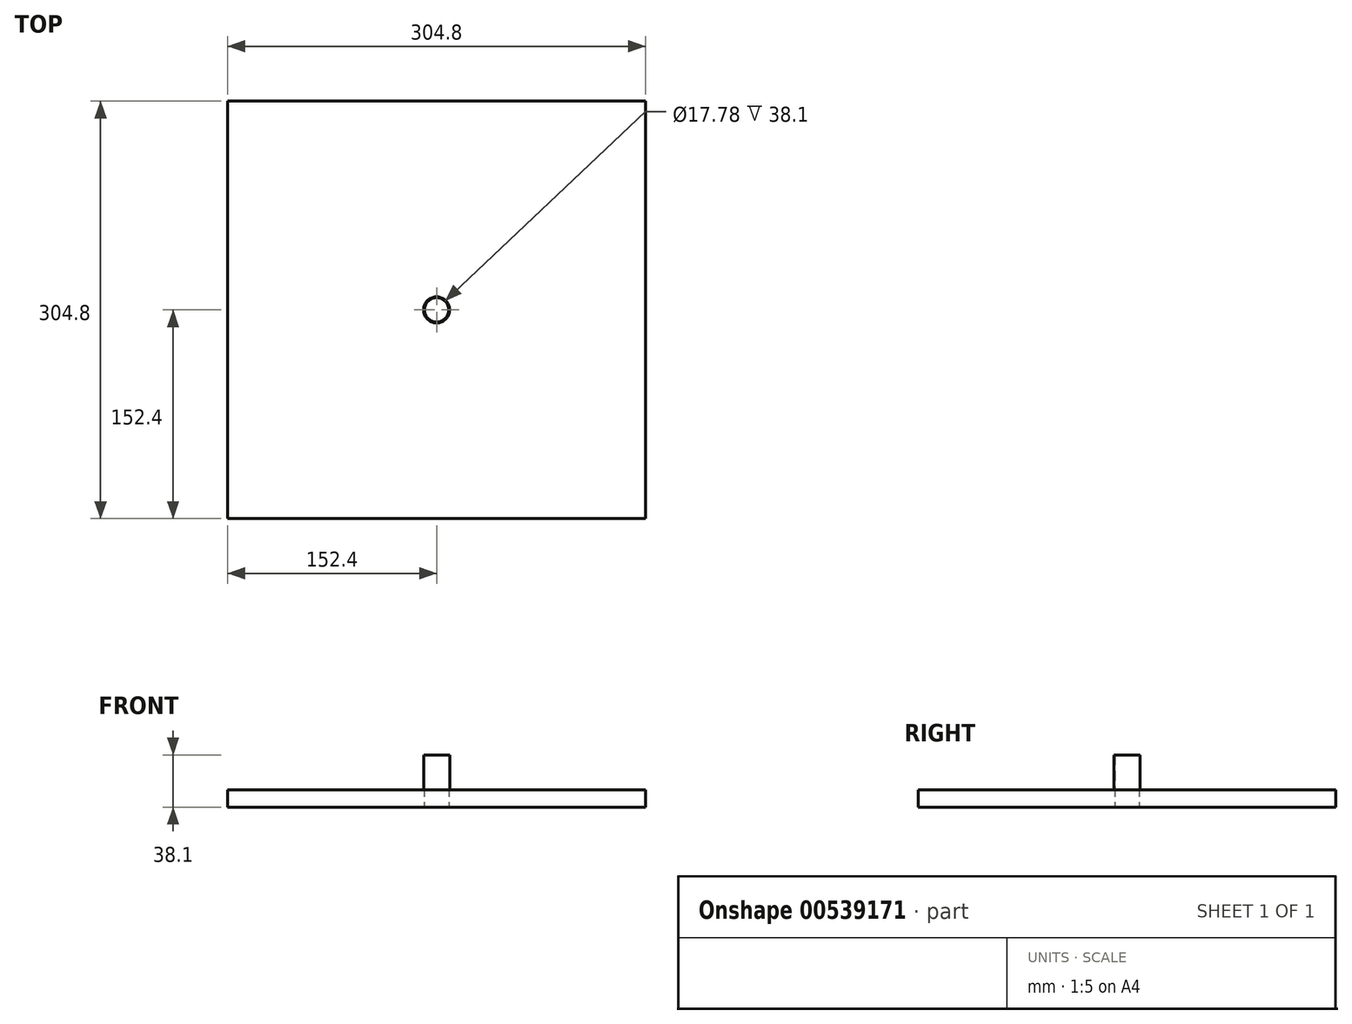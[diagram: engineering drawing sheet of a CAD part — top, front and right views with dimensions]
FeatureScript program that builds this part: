
annotation { "Feature Type Name" : "Feature", "Feature Type Description" : "" }
export const myFeature = defineFeature(function(context is Context, id is Id, definition is map)
    precondition{}
    {
        {
            var Q0;
            Q0=qCreatedBy(makeId("Top.planeOp"),FACE);
            var sketch = newSketch(context, id + "F0", { "sketchPlane" : qUnion([Q0])});
            skLineSegment(sketch, "E0.bottom", {"start": v(152.4, -152.4) * mm, "end": v(-152.4, -152.4) * mm});
            skLineSegment(sketch, "E0.top", {"start": v(152.4, 152.4) * mm, "end": v(-152.4, 152.4) * mm});
            skLineSegment(sketch, "E0.left", {"start": v(152.4, -152.4) * mm, "end": v(152.4, 152.4) * mm});
            skLineSegment(sketch, "E0.right", {"start": v(-152.4, -152.4) * mm, "end": v(-152.4, 152.4) * mm});
            skPoint(sketch, "E0.middle", {"position": v(0, 0) * mm});
            skSolve(sketch);
        }
        {
            var Q0;
            Q0 = qSketchRegion(id + "F0", true);
            extrude(context, id + "F1", {"entities" : qUnion([Q0]), "depth" : 12.7 * mm, "offsetDistance" : 25.4 * mm});
        }
        {
            var Q0;
            Q0=qCreatedBy(makeId("Top.planeOp"),FACE);
            var sketch = newSketch(context, id + "F2", { "sketchPlane" : qUnion([Q0])});
            skCircle(sketch, "E1", {"center": v(0, 0) * mm, "radius": 9.53 * mm});
            skSolve(sketch);
        }
        {
            var Q0;
            Q0 = qSketchRegion(id + "F2", true);
            extrude(context, id + "F3", {"entities" : qUnion([Q0]), "operationType" : NewBodyOperationType.REMOVE, "endBound" : BoundingType.SYMMETRIC, "oppositeDirection" : true, "depth" : 25.4 * mm, "offsetDistance" : 25.4 * mm});
        }
        {
            var Q0;
            Q0=qCreatedBy(makeId("Front.planeOp"),FACE);
            var sketch = newSketch(context, id + "F4", { "sketchPlane" : qUnion([Q0])});
            skLineSegment(sketch, "E2.bottom", {"start": v(0, 0) * mm, "end": v(9.52, 0) * mm});
            skLineSegment(sketch, "E2.top", {"start": v(0, 38.1) * mm, "end": v(9.52, 38.1) * mm});
            skLineSegment(sketch, "E2.left", {"start": v(0, 0) * mm, "end": v(0, 38.1) * mm});
            skLineSegment(sketch, "E2.right", {"start": v(9.52, 0) * mm, "end": v(9.52, 38.1) * mm});
            skSolve(sketch);
        }
        {
            var Q0;
            Q0 = qSketchRegion(id + "F4", true);
            var Q1;
            Q1=sQuery(id+"F4.wireOp",EDGE,"E2.left");
            revolve(context, id + "F5", {"operationType" : NewBodyOperationType.ADD, "entities" : qUnion([Q0]), "axis" : qUnion([Q1]), "revolveType" : RevolveType.FULL});
        }
        {
            var Q0;
            Q0=qCreatedBy(makeId("Top.planeOp"),FACE);
            var sketch = newSketch(context, id + "F6", { "sketchPlane" : qUnion([Q0])});
            skCircle(sketch, "E3", {"center": v(0, 0) * mm, "radius": 8.9 * mm});
            skSolve(sketch);
        }
        {
            var Q0;
            Q0 = qSketchRegion(id + "F6", true);
            extrude(context, id + "F7", {"entities" : qUnion([Q0]), "operationType" : NewBodyOperationType.REMOVE, "endBound" : BoundingType.THROUGH_ALL, "depth" : 25.4 * mm, "offsetDistance" : 25.4 * mm});
        }
    });
